# Revit family: QF_COMENDA_AC2EP5_L-R - Copia
name_source: partatom
category: Attrezzature speciali
revit_build: Autodesk Revit 2017 (Build: 20160225_1515(x64)
units: mm (PartAtom-declared; Revit-internal decimal feet)

## family parameters
Basato su piano di lavoro = No
Condiviso = No
Punto di calcolo locali = No
Quota connettore circolare = Usa diametro
Sempre verticale = Sì
Taglio con vuoti quando caricato = No
Tipo di parte = Normale

## types (1)
- QF_COMENDA_AC2EP5_L-R - Copia
    Altezza = 2040 mm  [stored 6.69291 ft]
    Altezza connessione acqua calda = 234 mm  [stored 0.767717 ft]
    Altezza connessione acqua fredda = 234 mm  [stored 0.767717 ft]
    Altezza connessione elettrica = 1615 mm  [stored 5.29856 ft]
    Altezza connessione scarico diretto = 170 mm  [stored 0.557743 ft]
    Codice assieme = 60BE03440
    Corrente di funzionamento normale = 56 A
    Descrizione = 600 mm PREWASH ZONE, 1150 mm WASH ZONE, 400 mm DOUBLE RINSE ZONE, 800 mm DRYING ZONE WITH INTEGRATED HEAT RECOVERY UNIT
    Diametro condotta acqua fredda = 19 mm
    Diametro condotto di evacuazione = 230 mm  [stored 0.754593 ft]
    Diametro dello scarico diretto di acqua = 100 mm
    Diametro raccordo acqua calda = 19 mm
    Flusso acqua fredda = 4.5 l/min
    Frequenza = 50 Hz
    Lunghezza = 2850 mm  [stored 9.35039 ft]
    Modello = AC2EP6N
    Numero dei poli = 3
    Omniclass numero e denominazione = 23.40.40.14 Food Service Equipment
    Peso netto = 320.00 kg
    Pessione minima acqua fredda = 2.0 barra
    Phase = 3
    Portata di evacuazione = 480.0 m³/h
    Potenza elettrica = 33860 W
    Potenza in CV = 4603.7
    Pressione minima acqua calda = 2.0 barra
    Produttore = Comenda
    Profondità = 790 mm  [stored 2.59186 ft]
    Protezione contro le sovracorrenti = 125 A
    Temperatura dell'aria evacuata = 35 °C
    Temperatura raccomandata per acqua calda  = 55 °C
    Temperatura raccomandata per acqua fredda  = 12 °C
    Tensione = 400 V
    Tipo di raccordo elettrico = Three-phase neutral
    URL = https://www.comenda.eu
    URL catalogo = https://www.comenda.eu

note: [stored X ft] marks values corroborated as IEEE doubles in the binary element streams (Revit-internal decimal feet)
